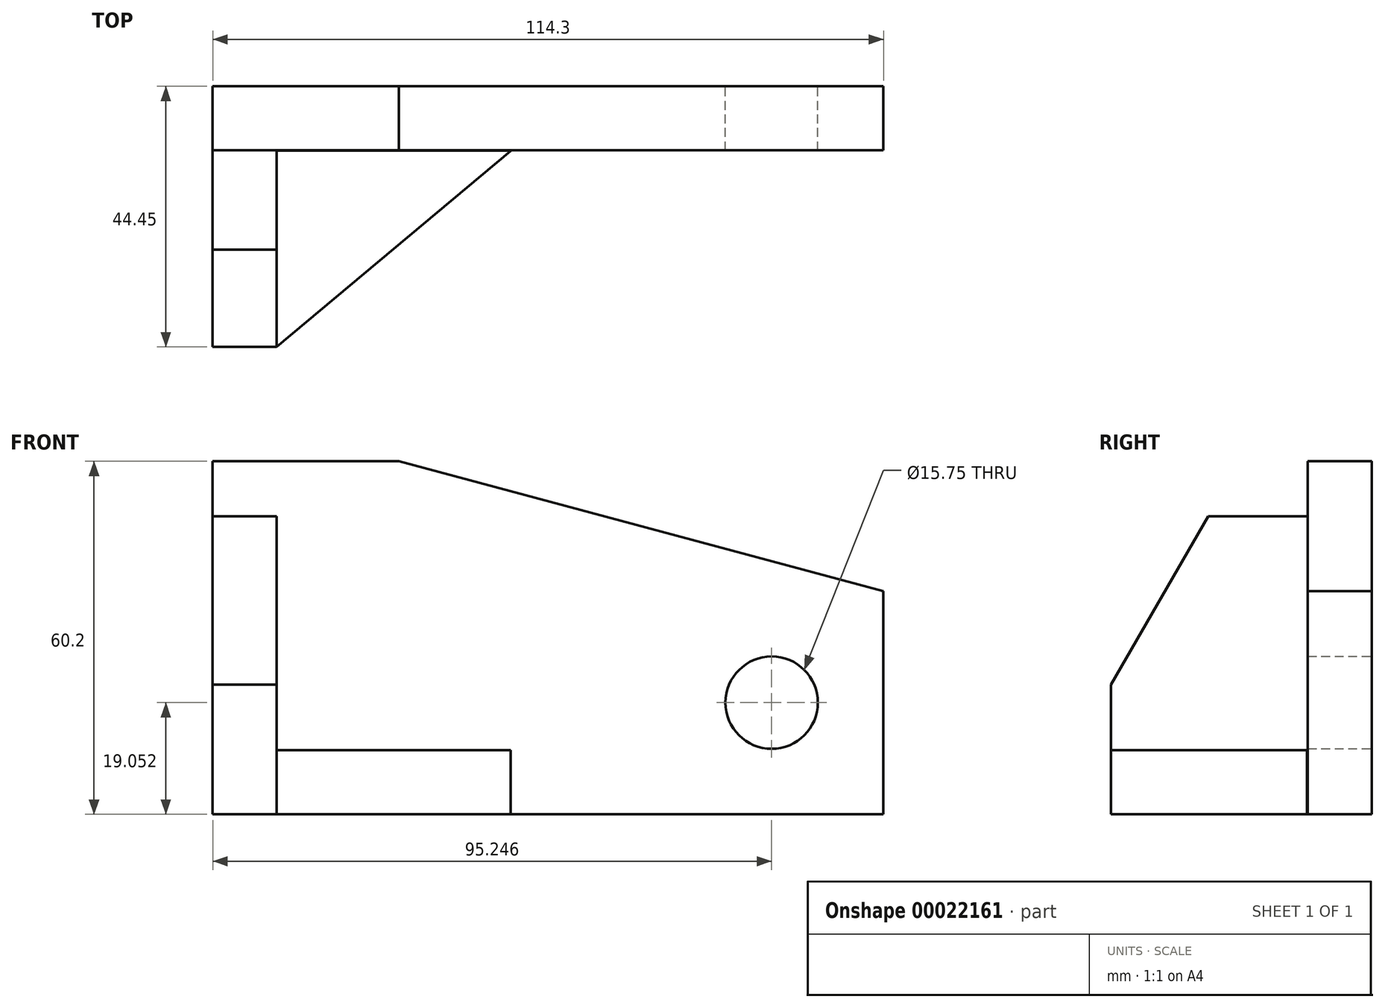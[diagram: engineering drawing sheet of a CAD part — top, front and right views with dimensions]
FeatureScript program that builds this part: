
annotation { "Feature Type Name" : "Feature", "Feature Type Description" : "" }
export const myFeature = defineFeature(function(context is Context, id is Id, definition is map)
    precondition{}
    {
        {
            var Q0;
            Q0=qCreatedBy(makeId("Front.planeOp"),FACE);
            var sketch = newSketch(context, id + "F0", { "sketchPlane" : qUnion([Q0])});
            skLineSegment(sketch, "E0.bottom", {"start": v(-17.72, 25.02) * mm, "end": v(-49.47, 25.02) * mm});
            skLineSegment(sketch, "E0.top", {"start": v(64.83, -35.18) * mm, "end": v(-49.47, -35.18) * mm});
            skLineSegment(sketch, "E0.left", {"start": v(64.83, 2.9) * mm, "end": v(64.83, -35.18) * mm});
            skLineSegment(sketch, "E0.right", {"start": v(-49.47, 25.02) * mm, "end": v(-49.47, -35.18) * mm});
            skLineSegment(sketch, "E1", {"start": v(-17.72, 25.02) * mm, "end": v(64.83, 2.9) * mm});
            skLineSegment(sketch, "E2", {"start": v(-49.47, 25.02) * mm, "end": v(-17.72, 25.02) * mm});
            skCircle(sketch, "E3", {"center": v(45.78, -16.13) * mm, "radius": 7.87 * mm});
            skSolve(sketch);
        }
        {
            var Q0;
            Q0 = qSketchRegion(id + "F0", true);
            extrude(context, id + "F1", {"entities" : qUnion([Q0]), "depth" : 10.92 * mm});
        }
        {
            var Q0;
            Q0=makeQuery(id+"F1.opExtrude","SWEPT_FACE",FACE,{"disambiguationData":[OSD([sQuery(id+"F0.wireOp",EDGE,"E0.right")])]});
            var sketch = newSketch(context, id + "F2", { "sketchPlane" : qUnion([Q0])});
            skLineSegment(sketch, "E4.bottom", {"start": v(10.92, -35.18) * mm, "end": v(44.45, -35.18) * mm});
            skLineSegment(sketch, "E4.top", {"start": v(10.92, 15.62) * mm, "end": v(27.88, 15.62) * mm});
            skLineSegment(sketch, "E4.left", {"start": v(10.92, -35.18) * mm, "end": v(10.92, 15.62) * mm});
            skLineSegment(sketch, "E4.right", {"start": v(44.45, -35.18) * mm, "end": v(44.45, -13.08) * mm});
            skLineSegment(sketch, "E5", {"start": v(44.45, -13.08) * mm, "end": v(44.45, -35.18) * mm});
            skLineSegment(sketch, "E6", {"start": v(44.45, -13.08) * mm, "end": v(27.88, 15.62) * mm});
            skSolve(sketch);
        }
        {
            var Q0;
            Q0=makeQuery(id+"F2.imprint","IMPRINT",FACE,{"disambiguationData":[TD([[makeQuery(id+"F2.imprint","IMPRINT",EDGE,{"derivedFrom":sQuery(id+"F2.wireOp",EDGE,"E4.bottom")}),1.0]])]});
            extrude(context, id + "F3", {"entities" : qUnion([Q0]), "oppositeDirection" : true, "depth" : 10.92 * mm});
        }
        {
            var Q0;
            Q0=makeQuery(id+"F3.opExtrude","SWEPT_FACE",FACE,{"disambiguationData":[OSD([sQuery(id+"F2.wireOp",EDGE,"E4.bottom")])]});
            var sketch = newSketch(context, id + "F4", { "sketchPlane" : qUnion([Q0])});
            skLineSegment(sketch, "E7", {"start": v(-38.55, 44.45) * mm, "end": v(1.33, 11.04) * mm});
            skLineSegment(sketch, "E8", {"start": v(1.33, 11.04) * mm, "end": v(-38.55, 10.92) * mm});
            skLineSegment(sketch, "E9", {"start": v(-38.55, 10.92) * mm, "end": v(-38.55, 44.45) * mm});
            skLineSegment(sketch, "E10", {"start": v(1.33, 11.04) * mm, "end": v(-49.47, 10.92) * mm});
            skSolve(sketch);
        }
        {
            var Q0;
            {var subQ3=sQuery(id+"F4.wireOp",EDGE,"E7");Q0=makeQuery(id+"F4.imprint","IMPRINT",FACE,{"disambiguationData":[TD([[makeQuery(id+"F4.imprint","IMPRINT",EDGE,{"derivedFrom":subQ3}),-1.0]])]});}
            extrude(context, id + "F5", {"entities" : qUnion([Q0]), "oppositeDirection" : true, "depth" : 10.92 * mm});
        }
    });
